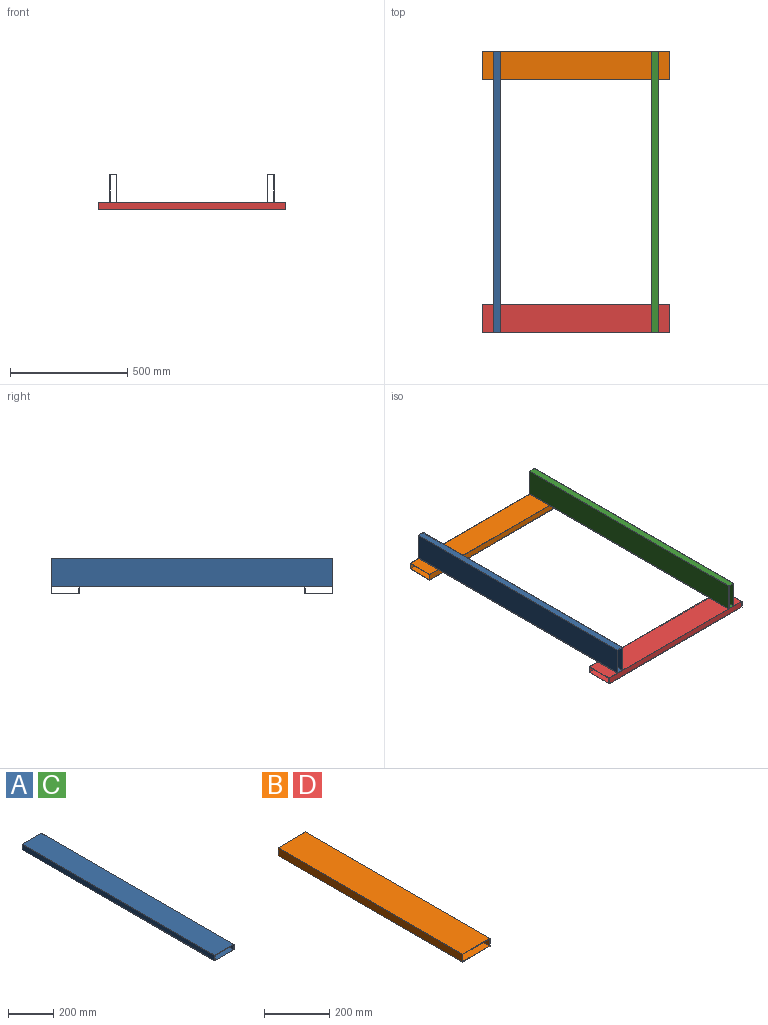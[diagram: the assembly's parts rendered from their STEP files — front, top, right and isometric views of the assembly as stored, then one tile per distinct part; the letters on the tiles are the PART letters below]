
ASSEMBLY  parts=4 mates=1
PART A: 10 faces, bbox 120x1200x30 mm
  f0: plane 1200x26.4mm, normal (1,0,0), area 31680mm2, adj f1,f7,f8,f9
  f1: plane 1200x116.4mm, normal (0,0,-1), area 139680mm2, adj f0,f2,f8,f9
  f2: plane 1200x26.4mm, normal (-1,0,0), area 31680mm2, adj f1,f7,f8,f9
  f3: plane 1200x30mm, normal (-1,0,0), area 36000mm2, adj f4,f6,f8,f9
  f4: plane 1200x120mm, normal (0,0,-1), area 144000mm2, adj f3,f5,f8,f9
  f5: plane 1200x30mm, normal (1,0,0), area 36000mm2, adj f4,f6,f8,f9
  f6: plane 1200x120mm, normal (0,0,1), area 144000mm2, adj f3,f5,f8,f9
  f7: plane 1200x116.4mm, normal (0,0,1), area 139680mm2, adj f0,f2,f8,f9
  f8: plane 120x30mm, normal (0,-1,0), area 527mm2, adj f0,f1,f2,f3,f4,f5,f6,f7
  f9: plane 120x30mm, normal (0,1,0), area 527mm2, adj f0,f1,f2,f3,f4,f5,f6,f7
PART B: 10 faces, bbox 120x800x30 mm
  f0: plane 800x26.4mm, normal (1,0,0), area 21120mm2, adj f1,f7,f8,f9
  f1: plane 800x116.4mm, normal (0,0,-1), area 93120mm2, adj f0,f2,f8,f9
  f2: plane 800x26.4mm, normal (-1,0,0), area 21120mm2, adj f1,f7,f8,f9
  f3: plane 800x30mm, normal (-1,0,0), area 24000mm2, adj f4,f6,f8,f9
  f4: plane 800x120mm, normal (0,0,-1), area 96000mm2, adj f3,f5,f8,f9
  f5: plane 800x30mm, normal (1,0,0), area 24000mm2, adj f4,f6,f8,f9
  f6: plane 800x120mm, normal (0,0,1), area 96000mm2, adj f3,f5,f8,f9
  f7: plane 800x116.4mm, normal (0,0,1), area 93120mm2, adj f0,f2,f8,f9
  f8: plane 120x30mm, normal (0,-1,0), area 527mm2, adj f0,f1,f2,f3,f4,f5,f6,f7
  f9: plane 120x30mm, normal (0,1,0), area 527mm2, adj f0,f1,f2,f3,f4,f5,f6,f7
PART C: same geometry as A
PART D: same geometry as B
PLACE A rot(axis=(0,-1,0),90deg) t=(-280.17,876.29,-49.79)mm fixed
PLACE B rot(axis=(0,0,1),90deg) t=(-360.17,756.29,-79.79)mm
PLACE C rot(axis=(0,-1,0),90deg) t=(389.83,876.29,-49.79)mm
PLACE D rot(axis=(0,0,1),90deg) t=(-360.17,-323.71,-79.79)mm
MATE fastened D.f6 <-> A.f3  axis (0,0,1) through (39.83,-323.71,-49.79)mm
